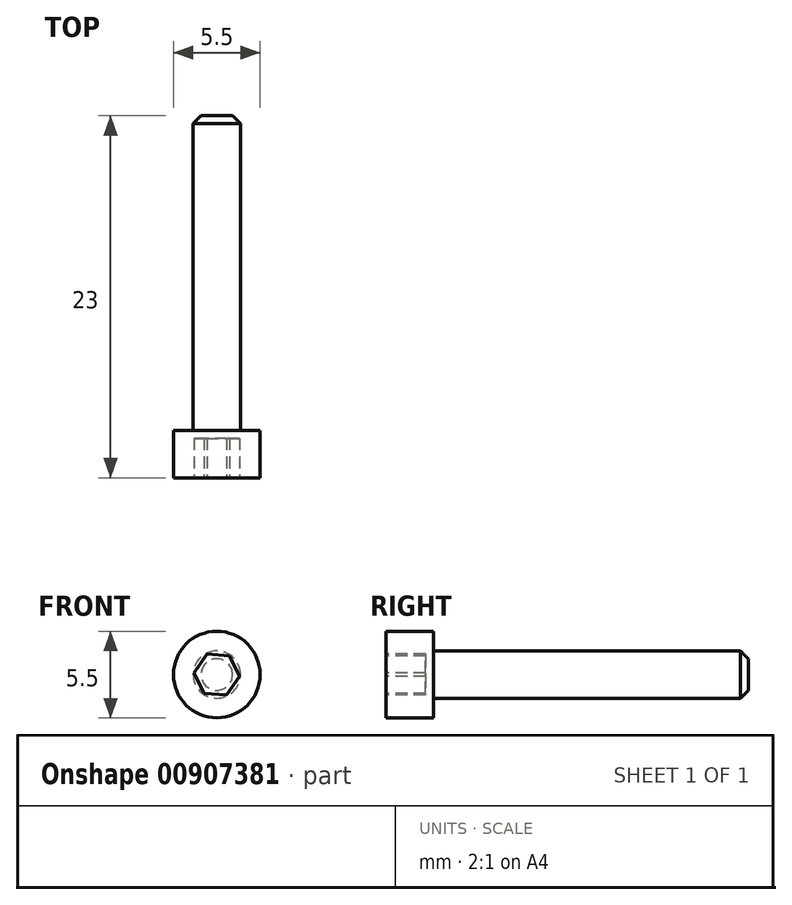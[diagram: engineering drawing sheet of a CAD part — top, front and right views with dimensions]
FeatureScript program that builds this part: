
annotation { "Feature Type Name" : "Feature", "Feature Type Description" : "" }
export const myFeature = defineFeature(function(context is Context, id is Id, definition is map)
    precondition{}
    {
        {
            assignVariable(context, id + "F0", {"name" : "Metric", "anyValue" : 3});
        }
        {
            assignVariable(context, id + "F1", {"name" : "Lenght", "anyValue" : 20});
        }
        {
            assignVariable(context, id + "F2", {"name" : "k", "anyValue" : [0, 1, 2, 3, 4, 5, 6, 0, 8][getVariable(context, 'Metric')]});
        }
        {
            var Q0;
            Q0=qCreatedBy(makeId("Front.planeOp"),FACE);
            var sketch = newSketch(context, id + "F3", { "sketchPlane" : qUnion([Q0])});
            skCircle(sketch, "E0", {"center": v(0, 0) * mm, "radius": 2.75 * mm});
            skSolve(sketch);
        }
        {
            var Q0;
            Q0=qSketchRegion(id+"F3",true);
            extrude(context, id + "F4", {"entities" : qUnion([Q0]), "depth" : (getVariable(context, 'k')) * mm, "offsetDistance" : 25 * mm});
        }
        {
            var Q0;
            Q0=makeQuery(id+"F4.opExtrude","CAP_FACE",FACE,{"disambiguationData":[OSD([sQuery(id+"F3.wireOp",EDGE,"E0")])],"isStart":true});
            var sketch = newSketch(context, id + "F5", { "sketchPlane" : qUnion([Q0])});
            skCircle(sketch, "E1", {"center": v(0, 0) * mm, "radius": 1.5 * mm});
            skSolve(sketch);
        }
        {
            var Q0;
            Q0=qSketchRegion(id+"F5",true);
            extrude(context, id + "F6", {"entities" : qUnion([Q0]), "operationType" : NewBodyOperationType.ADD, "depth" : (getVariable(context, 'Lenght')) * mm, "offsetDistance" : 25 * mm});
        }
        {
            var Q0;
            Q0=makeQuery(id+"F4.opExtrude","CAP_FACE",FACE,{"disambiguationData":[OSD([sQuery(id+"F3.wireOp",EDGE,"E0")])],"isStart":false});
            var sketch = newSketch(context, id + "F7", { "sketchPlane" : qUnion([Q0])});
            skCircle(sketch, "E2.cCircle", {"center": v(0, 0) * mm, "radius": 1.25 * mm, "construction": true});
            skLineSegment(sketch, "E2.0", {"start": v(-1.44, 0.11) * mm, "end": v(-0.62, 1.3) * mm});
            skLineSegment(sketch, "E2.1", {"start": v(-0.62, 1.3) * mm, "end": v(0.81, 1.2) * mm});
            skLineSegment(sketch, "E2.2", {"start": v(0.81, 1.2) * mm, "end": v(1.44, -0.11) * mm});
            skLineSegment(sketch, "E2.3", {"start": v(1.44, -0.11) * mm, "end": v(0.62, -1.3) * mm});
            skLineSegment(sketch, "E2.4", {"start": v(0.62, -1.3) * mm, "end": v(-0.81, -1.2) * mm});
            skLineSegment(sketch, "E2.5", {"start": v(-0.81, -1.2) * mm, "end": v(-1.44, 0.11) * mm});
            skPoint(sketch, "E2.0.midPoint", {"position": v(-1.03, 0.7) * mm});
            skSolve(sketch);
        }
        {
            var Q0;
            Q0=qSketchRegion(id+"F7",true);
            extrude(context, id + "F8", {"entities" : qUnion([Q0]), "operationType" : NewBodyOperationType.REMOVE, "oppositeDirection" : true, "depth" : (getVariable(context, 'k') - 0.5) * mm, "offsetDistance" : 25 * mm});
        }
        {
            var Q0;
            Q0=makeQuery(id+"F6.opExtrude","CAP_EDGE",EDGE,{"disambiguationData":[OSD([sQuery(id+"F5.wireOp",EDGE,"E1")])],"isStart":false});
            chamfer(context, id + "F9", {"entities" : qUnion([Q0]), "width" : 0.5 * mm, "tangentPropagation" : true});
        }
    });
